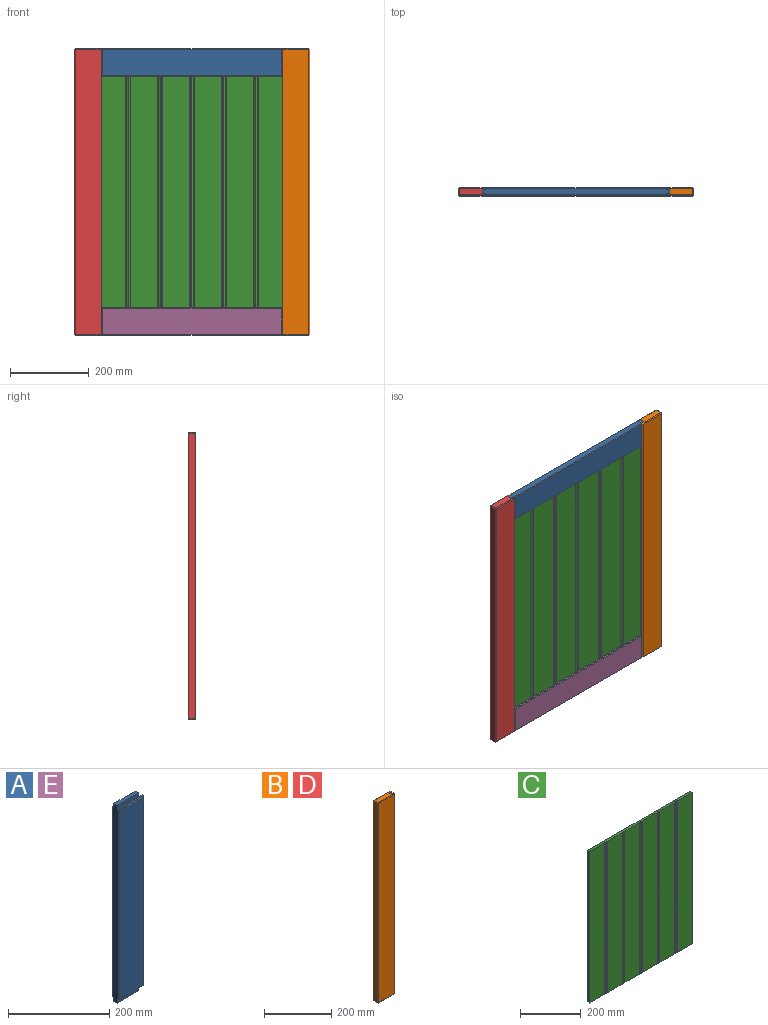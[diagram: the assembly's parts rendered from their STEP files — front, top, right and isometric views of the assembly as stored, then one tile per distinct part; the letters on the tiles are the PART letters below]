
ASSEMBLY  parts=5 mates=12
PART A: 26 faces, bbox 70x20x478 mm
  f0: plane 478x16mm, normal (-1,0,0), area 7508mm2, adj f7,f8,f10,f11,f12,f13,f14,f15
  f1: plane 454x66mm, normal (0,-1,0), area 29964mm2, adj f18,f19,f20,f21
  f2: plane 458x3.5mm, normal (1,0,0), area 1603mm2, adj f3,f10,f17,f21
  f3: plane 458x10mm, normal (0,1,0), area 4580mm2, adj f2,f9,f10,f17
  f4: plane 458x10mm, normal (0,-1,0), area 4580mm2, adj f5,f9,f12,f15
  f5: plane 458x3.5mm, normal (1,0,0), area 1603mm2, adj f4,f12,f15,f22
  f6: plane 454x66mm, normal (0,1,0), area 29964mm2, adj f22,f23,f24,f25
  f7: plane 60x9mm, normal (0,0,1), area 540mm2, adj f0,f9,f14,f16
  f8: plane 60x9mm, normal (0,0,-1), area 540mm2, adj f0,f9,f11,f13
  f9: plane 478x9mm, normal (1,0,0), area 4302mm2, adj f3,f4,f7,f8,f11,f13,f14,f16
  f10: plane 70x3.5mm, normal (0,0,-1), area 245mm2, adj f0,f2,f3,f11,f20
  f11: plane 60x10mm, normal (0,-1,0), area 600mm2, adj f0,f8,f9,f10
  f12: plane 70x3.5mm, normal (0,0,-1), area 245mm2, adj f0,f4,f5,f13,f24
  f13: plane 60x10mm, normal (0,1,0), area 600mm2, adj f0,f8,f9,f12
  f14: plane 60x10mm, normal (0,1,0), area 600mm2, adj f0,f7,f9,f15
  f15: plane 70x3.5mm, normal (0,0,1), area 245mm2, adj f0,f4,f5,f14,f23
  f16: plane 60x10mm, normal (0,-1,0), area 600mm2, adj f0,f7,f9,f17
  f17: plane 70x3.5mm, normal (0,0,1), area 245mm2, adj f0,f2,f3,f16,f19
  f18: plane 458x2mm, normal (-0.71,-0.71,0), area 1289.8mm2, adj f0,f1,f19,f20
  f19: plane 70x2mm, normal (0,-0.71,0.71), area 192.3mm2, adj f1,f17,f18,f21
  f20: plane 70x2mm, normal (0,-0.71,-0.71), area 192.3mm2, adj f1,f10,f18,f21
  f21: plane 458x2mm, normal (0.71,-0.71,0), area 1289.8mm2, adj f1,f2,f19,f20
  f22: plane 458x2mm, normal (0.71,0.71,0), area 1289.8mm2, adj f5,f6,f23,f24
  f23: plane 70x2mm, normal (0,0.71,0.71), area 192.3mm2, adj f6,f15,f22,f25
  f24: plane 70x2mm, normal (0,0.71,-0.71), area 192.3mm2, adj f6,f12,f22,f25
  f25: plane 458x2mm, normal (-0.71,0.71,0), area 1289.8mm2, adj f0,f6,f23,f24
PART B: 24 faces, bbox 70x20x729 mm
  f0: plane 725x16mm, normal (-1,0,0), area 11600mm2, adj f14,f15,f18,f19
  f1: plane 725x66mm, normal (0,-1,0), area 47850mm2, adj f10,f11,f13,f14
  f2: plane 729x3.5mm, normal (1,0,0), area 2551.5mm2, adj f3,f8,f9,f11
  f3: plane 729x10mm, normal (0,1,0), area 7290mm2, adj f2,f4,f8,f9
  f4: plane 729x9mm, normal (1,0,0), area 6561mm2, adj f3,f5,f8,f9
  f5: plane 729x10mm, normal (0,-1,0), area 7290mm2, adj f4,f6,f8,f9
  f6: plane 729x3.5mm, normal (1,0,0), area 2551.5mm2, adj f5,f8,f9,f22
  f7: plane 725x66mm, normal (0,1,0), area 47850mm2, adj f19,f20,f22,f23
  f8: plane 68x16mm, normal (0,0,1), area 998mm2, adj f2,f3,f4,f5,f6,f13,f18,f23
  f9: plane 68x16mm, normal (0,0,-1), area 998mm2, adj f2,f3,f4,f5,f6,f10,f15,f20
  f10: plane 68x2mm, normal (0,-0.71,-0.71), area 189.5mm2, adj f1,f9,f11,f12
  f11: plane 729x2mm, normal (0.71,-0.71,0), area 2056.3mm2, adj f1,f2,f10,f13
  f12: plane 2x2mm, normal (-0.58,-0.58,-0.58), area 3.5mm2, adj f10,f14,f15
  f13: plane 68x2mm, normal (0,-0.71,0.71), area 189.5mm2, adj f1,f8,f11,f16
  f14: plane 725x2mm, normal (-0.71,-0.71,0), area 2050.6mm2, adj f0,f1,f12,f16
  f15: plane 16x2mm, normal (-0.71,0,-0.71), area 45.3mm2, adj f0,f9,f12,f17
  f16: plane 2x2mm, normal (-0.58,-0.58,0.58), area 3.5mm2, adj f13,f14,f18
  f17: plane 2x2mm, normal (-0.58,0.58,-0.58), area 3.5mm2, adj f15,f19,f20
  f18: plane 16x2mm, normal (-0.71,0,0.71), area 45.3mm2, adj f0,f8,f16,f21
  f19: plane 725x2mm, normal (-0.71,0.71,0), area 2050.6mm2, adj f0,f7,f17,f21
  f20: plane 68x2mm, normal (0,0.71,-0.71), area 189.5mm2, adj f7,f9,f17,f22
  f21: plane 2x2mm, normal (-0.58,0.58,0.58), area 3.5mm2, adj f18,f19,f23
  f22: plane 729x2mm, normal (0.71,0.71,0), area 2056.3mm2, adj f6,f7,f20,f23
  f23: plane 68x2mm, normal (0,0.71,0.71), area 189.5mm2, adj f7,f8,f21,f22
PART C: 41 faces, bbox 478x9x609 mm
  f0: plane 478x9mm, normal (0,0,1), area 4256.6mm2, adj f1,f2,f3,f4,f5,f6,f8,f9
  f1: plane 609x71mm, normal (0,-1,0), area 43239mm2, adj f0,f6,f7,f29
  f2: plane 609x69mm, normal (0,-1,0), area 42021mm2, adj f0,f7,f25,f28
  f3: plane 609x69mm, normal (0,-1,0), area 42021mm2, adj f0,f7,f21,f24
  f4: plane 609x69mm, normal (0,-1,0), area 42021mm2, adj f0,f7,f17,f20
  f5: plane 609x69mm, normal (0,-1,0), area 42021mm2, adj f0,f7,f13,f16
  f6: plane 609x9mm, normal (-1,0,0), area 5481mm2, adj f0,f1,f7,f10
  f7: plane 478x9mm, normal (0,0,-1), area 4256.6mm2, adj f1,f2,f3,f4,f5,f6,f8,f9
  f8: plane 609x9mm, normal (1,0,0), area 5481mm2, adj f0,f7,f9,f10
  f9: plane 609x71mm, normal (0,-1,0), area 43239mm2, adj f0,f7,f8,f12
  f10: plane 609x478mm, normal (0,1,0), area 291102mm2, adj f0,f6,f7,f8
  f11: plane 609x0.54mm, normal (0.71,-0.71,0), area 461.2mm2, adj f0,f7,f12,f32
  f12: plane 609x2mm, normal (-0.71,-0.71,0), area 1722.5mm2, adj f0,f7,f9,f11
  f13: plane 609x2mm, normal (0.71,-0.71,0), area 1722.5mm2, adj f0,f5,f7,f14
  f14: plane 609x0.54mm, normal (-0.71,-0.71,0), area 461.2mm2, adj f0,f7,f13,f31
  f15: plane 609x0.54mm, normal (0.71,-0.71,0), area 461.2mm2, adj f0,f7,f16,f34
  f16: plane 609x2mm, normal (-0.71,-0.71,0), area 1722.5mm2, adj f0,f5,f7,f15
  f17: plane 609x2mm, normal (0.71,-0.71,0), area 1722.5mm2, adj f0,f4,f7,f18
  f18: plane 609x0.54mm, normal (-0.71,-0.71,0), area 461.2mm2, adj f0,f7,f17,f33
  f19: plane 609x0.54mm, normal (0.71,-0.71,0), area 461.2mm2, adj f0,f7,f20,f36
  f20: plane 609x2mm, normal (-0.71,-0.71,0), area 1722.5mm2, adj f0,f4,f7,f19
  f21: plane 609x2mm, normal (0.71,-0.71,0), area 1722.5mm2, adj f0,f3,f7,f22
  f22: plane 609x0.54mm, normal (-0.71,-0.71,0), area 461.2mm2, adj f0,f7,f21,f35
  f23: plane 609x0.54mm, normal (0.71,-0.71,0), area 461.2mm2, adj f0,f7,f24,f38
  f24: plane 609x2mm, normal (-0.71,-0.71,0), area 1722.5mm2, adj f0,f3,f7,f23
  f25: plane 609x2mm, normal (0.71,-0.71,0), area 1722.5mm2, adj f0,f2,f7,f26
  f26: plane 609x0.54mm, normal (-0.71,-0.71,0), area 461.2mm2, adj f0,f7,f25,f37
  f27: plane 609x0.54mm, normal (0.71,-0.71,0), area 461.2mm2, adj f0,f7,f28,f40
  f28: plane 609x2mm, normal (-0.71,-0.71,0), area 1722.5mm2, adj f0,f2,f7,f27
  f29: plane 609x2mm, normal (0.71,-0.71,0), area 1722.5mm2, adj f0,f1,f7,f30
  f30: plane 609x0.54mm, normal (-0.71,-0.71,0), area 461.2mm2, adj f0,f7,f29,f39
  f31: cylinder r=5mm len=609mm, axis (0,0,1), area 2348.3mm2, adj f0,f7,f14,f32
  f32: cylinder r=5mm len=609mm, axis (0,0,1), area 2348.3mm2, adj f0,f7,f11,f31
  f33: cylinder r=5mm len=609mm, axis (0,0,1), area 2348.3mm2, adj f0,f7,f18,f34
  f34: cylinder r=5mm len=609mm, axis (0,0,1), area 2348.3mm2, adj f0,f7,f15,f33
  f35: cylinder r=5mm len=609mm, axis (0,0,1), area 2348.3mm2, adj f0,f7,f22,f36
  f36: cylinder r=5mm len=609mm, axis (0,0,1), area 2348.3mm2, adj f0,f7,f19,f35
  f37: cylinder r=5mm len=609mm, axis (0,0,1), area 2348.3mm2, adj f0,f7,f26,f38
  f38: cylinder r=5mm len=609mm, axis (0,0,1), area 2348.3mm2, adj f0,f7,f23,f37
  f39: cylinder r=5mm len=609mm, axis (0,0,1), area 2348.3mm2, adj f0,f7,f30,f40
  f40: cylinder r=5mm len=609mm, axis (0,0,1), area 2348.3mm2, adj f0,f7,f27,f39
PART D: same geometry as B
PART E: same geometry as A
PLACE A rot(axis=(0.71,0,-0.71),180deg) t=(308.19,333.39,702.19)mm
PLACE B rot(axis=(0,0,1),180deg) t=(368.19,333.39,-26.81)mm
PLACE C t=(-169.81,327.89,33.19)mm
PLACE D t=(-229.81,313.39,-26.81)mm
PLACE E rot(axis=(0,-1,0),90deg) t=(308.19,313.39,-26.81)mm
MATE planar D.f4 <-> C.f6  axis (1,0,0) through (-169.81,323.39,337.69)mm
MATE planar A.f6 <-> B.f7  axis (0,-1,0) through (69.19,313.39,667.19)mm
MATE planar C.f1 <-> D.f3  axis (0,-1,0) through (-134.31,318.89,337.69)mm
MATE planar D.f1 <-> A.f6  axis (0,-1,0) through (-194.81,313.39,337.69)mm
MATE planar A.f17 <-> D.f2  axis (-1,0,0) through (-159.81,329.64,667.19)mm
MATE planar A.f0 <-> D.f8  axis (0,0,1) through (69.19,323.39,702.19)mm
MATE planar E.f0 <-> D.f9  axis (0,0,-1) through (69.19,323.39,-26.81)mm
MATE planar C.f7 <-> E.f9  axis (0,0,-1) through (69.19,323.43,33.19)mm
MATE planar A.f10 <-> B.f2  axis (1,0,0) through (298.19,329.64,667.19)mm
MATE planar B.f8 <-> A.f0  axis (0,0,1) through (334.8,323.39,702.19)mm
MATE planar E.f1 <-> B.f7  axis (0,-1,0) through (69.19,313.39,8.19)mm
MATE planar E.f17 <-> D.f2  axis (-1,0,0) through (-159.81,318.89,3.19)mm
